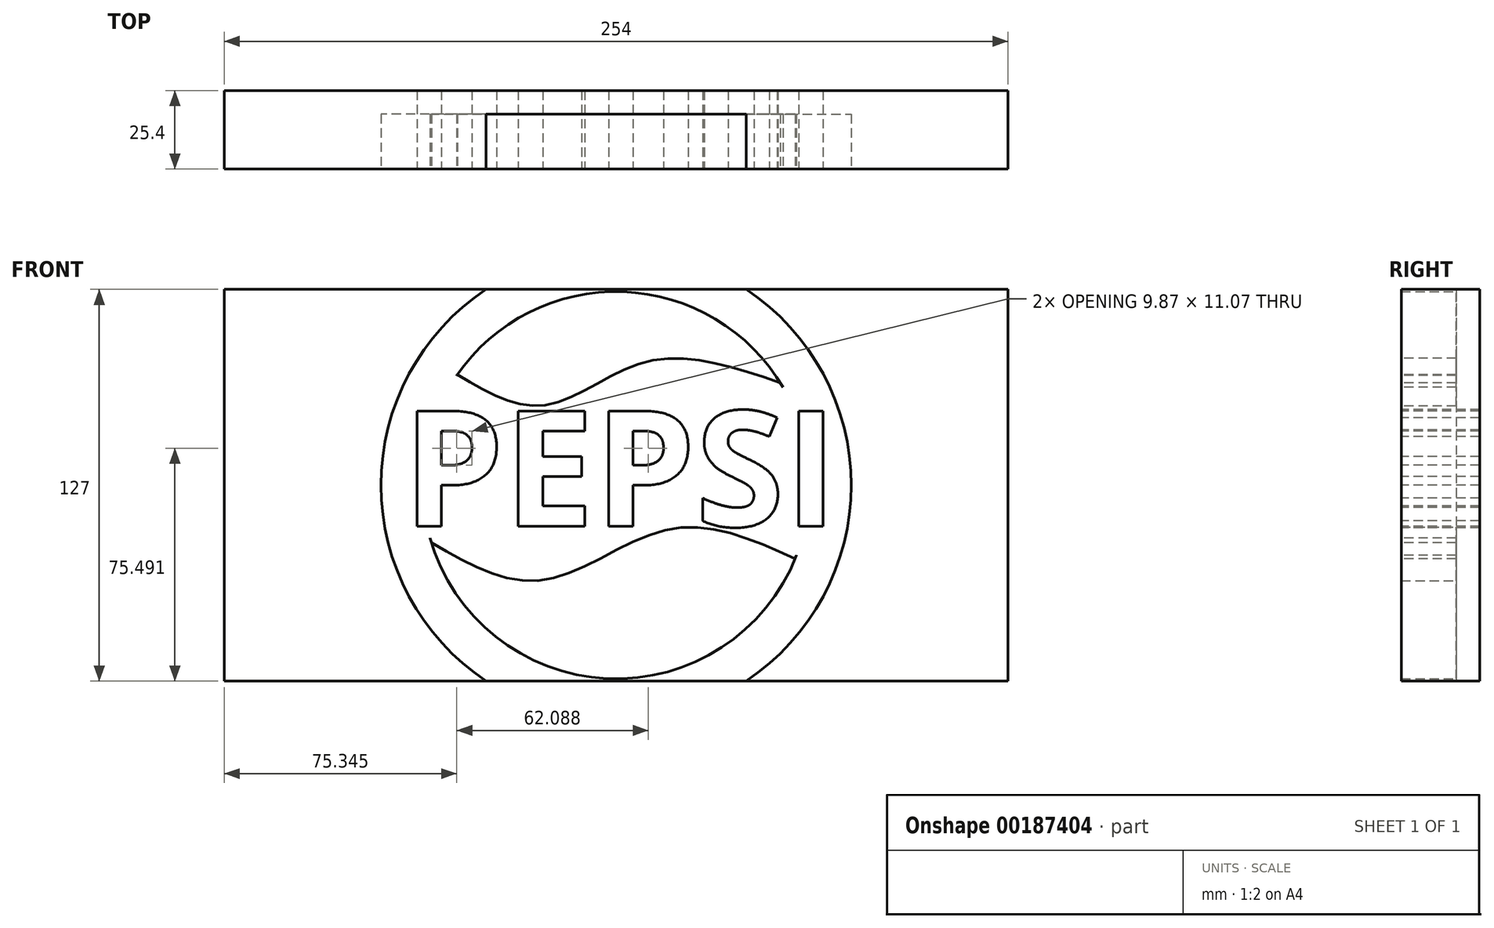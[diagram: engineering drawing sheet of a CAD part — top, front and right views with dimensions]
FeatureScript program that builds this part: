
annotation { "Feature Type Name" : "Feature", "Feature Type Description" : "" }
export const myFeature = defineFeature(function(context is Context, id is Id, definition is map)
    precondition{}
    {
        {
            var Q0;
            Q0=qCreatedBy(makeId("Front.planeOp"),FACE);
            var sketch = newSketch(context, id + "F0", { "sketchPlane" : qUnion([Q0])});
            skLineSegment(sketch, "E0.bottom", {"start": v(0, 0) * mm, "end": v(254, 0) * mm});
            skLineSegment(sketch, "E0.top", {"start": v(0, -127) * mm, "end": v(254, -127) * mm});
            skLineSegment(sketch, "E0.left", {"start": v(0, 0) * mm, "end": v(0, -127) * mm});
            skLineSegment(sketch, "E0.right", {"start": v(254, 0) * mm, "end": v(254, -127) * mm});
            skSolve(sketch);
        }
        {
            var Q0;
            Q0 = qSketchRegion(id + "F0", true);
            extrude(context, id + "F1", {"entities" : qUnion([Q0]), "depth" : 25.4 * mm});
        }
        {
            var Q0;
            Q0=makeQuery(id+"F1.opExtrude","CAP_FACE",FACE,{"disambiguationData":[OSD([sQuery(id+"F0.wireOp",EDGE,"E0.bottom"),sQuery(id+"F0.wireOp",EDGE,"E0.top"),sQuery(id+"F0.wireOp",EDGE,"E0.left"),sQuery(id+"F0.wireOp",EDGE,"E0.right")])],"isStart":false});
            var sketch = newSketch(context, id + "F2", { "sketchPlane" : qUnion([Q0])});
            skCircle(sketch, "E1", {"center": v(127, -63.5) * mm, "radius": 76.2 * mm});
            skPoint(sketch, "E1.centerSnap0", {"position": v(127, -127) * mm});
            skPoint(sketch, "E1.centerSnap1", {"position": v(0, -63.5) * mm});
            skSolve(sketch);
        }
        {
            var Q0;
            Q0 = qSketchRegion(id + "F2", true);
            extrude(context, id + "F3", {"entities" : qUnion([Q0]), "operationType" : NewBodyOperationType.REMOVE, "oppositeDirection" : true, "depth" : 17.78 * mm});
        }
        {
            var Q0;
            Q0=makeQuery(id+"F3.boolean.opBoolean","COPY",FACE,{"derivedFrom":makeQuery(id+"F3.opExtrude","CAP_FACE",FACE,{"disambiguationData":[OSD([sQuery(id+"F2.wireOp",EDGE,"E1")])],"isStart":false})});
            var sketch = newSketch(context, id + "F4", { "sketchPlane" : qUnion([Q0])});
            skCircle(sketch, "E2", {"center": v(127, -63.5) * mm, "radius": 62.74 * mm});
            skSolve(sketch);
        }
        {
            var Q0;
            Q0 = qSketchRegion(id + "F4", true);
            extrude(context, id + "F5", {"entities" : qUnion([Q0]), "operationType" : NewBodyOperationType.ADD, "depth" : 17.78 * mm});
        }
        {
            var Q0;
            Q0=makeQuery(id+"F5.opExtrude","CAP_FACE",FACE,{"disambiguationData":[OSD([sQuery(id+"F4.wireOp",EDGE,"E2")])],"isStart":false});
            var sketch = newSketch(context, id + "F6", { "sketchPlane" : qUnion([Q0])});
            skSolve(sketch);
        }
        {
            var Q0;
            Q0=makeQuery(id+"F6.imprint","IMPRINT",FACE,{"disambiguationData":[TD([[makeQuery(id+"F6.imprint","IMPRINT",EDGE,{"derivedFrom":makeQuery(id+"F5.opExtrude","CAP_EDGE",EDGE,{"disambiguationData":[OSD([sQuery(id+"F4.wireOp",EDGE,"E2")])],"isStart":false})}),1.0]])]});
            var sketch = newSketch(context, id + "F7", { "sketchPlane" : qUnion([Q0])});
            skFitSpline(sketch, "E3", {"points": [v(180.17, -30.29) * mm, v(137.14, -23.37) * mm, v(103.97, -37.58) * mm, v(75.54, -27.63) * mm], "startDerivative": vector(-122.22, 41.57) * mm, "endDerivative": vector(-93.2, 55.78) * mm});
            skFitSpline(sketch, "E4", {"points": [v(185.02, -87.3) * mm, v(144.45, -77.73) * mm, v(103.5, -94.22) * mm, v(67.17, -82.2) * mm], "startDerivative": vector(-120.96, 54.57) * mm, "endDerivative": vector(-111.5, 64.3) * mm});
            skArc(sketch, "E5", {"start": v(75.54, -27.63) * mm, "mid": v(64.57, -53.88) * mm, "end": v(67.17, -82.2) * mm});
            skArc(sketch, "E6", {"start": v(185.02, -87.3) * mm, "mid": v(189.9, -58.17) * mm, "end": v(180.17, -30.29) * mm});
            skSolve(sketch);
        }
        {
            var Q0;
            Q0 = qSketchRegion(id + "F7", true);
            extrude(context, id + "F8", {"entities" : qUnion([Q0]), "operationType" : NewBodyOperationType.REMOVE, "oppositeDirection" : true, "depth" : 17.78 * mm});
        }
        {
            var Q0;
            Q0=makeQuery(id+"F6.imprint","IMPRINT",FACE,{"disambiguationData":[TD([[makeQuery(id+"F6.imprint","IMPRINT",EDGE,{"derivedFrom":makeQuery(id+"F5.opExtrude","CAP_EDGE",EDGE,{"disambiguationData":[OSD([sQuery(id+"F4.wireOp",EDGE,"E2")])],"isStart":false})}),1.0]])]});
            var sketch = newSketch(context, id + "F9", { "sketchPlane" : qUnion([Q0])});
            skText(sketch, "E7", { "text": "PEPSI", "fontName": "OpenSans-Bold.ttf"});
            const initialGuessF9  = {"E7": [0.0578, -0.0768, 1, 0, 0.03763]};
            skSetInitialGuess(sketch, initialGuessF9);
            skSolve(sketch);
        }
        {
            var Q0;
            Q0 = qSketchRegion(id + "F9", true);
            extrude(context, id + "F10", {"entities" : qUnion([Q0]), "oppositeDirection" : true, "depth" : 25.4 * mm});
        }
    });
